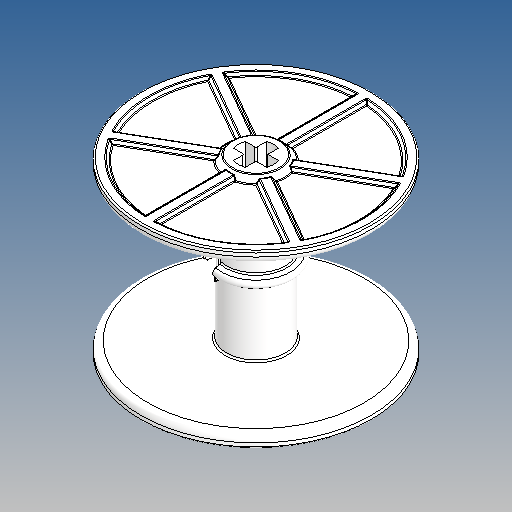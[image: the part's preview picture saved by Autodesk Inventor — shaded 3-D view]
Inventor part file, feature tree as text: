
AUTODESK INVENTOR PART (.ipt)
format: ipt  version: 2025 (Build 290162010, 162A)  size: 1,663,488 bytes
history: native  units: mm
features: fillet x5, sketch x4, extrude x3, pattern_circular x2, revolve x1, mirror x1
ambient origin geometry x8: Origin, YZ Plane, XZ Plane, XY Plane, X Axis, Y Axis, Z Axis, Center Point
bodies: Volumenkörper1 (feature_tree)
feature tree (16):
  revolve  "Umdrehung1"
  extrude  "Extrusion1"  Depth=8.0mm
  fillet  "Rundung1"  Radius=9.652752mm
  pattern_circular  "Runde Anordnung1"  [2 undecoded]
  fillet  "Rundung2"  Radius=0.75mm
  extrude  "Extrusion2"  Depth=10.0mm
  pattern_circular  "Runde Anordnung2"  [2 undecoded]
  fillet  "Rundung3"  Radius=1.2mm
  extrude  "Extrusion3"  TaperAngle=45.0deg  [1 undecoded]
  fillet  "Rundung4"  [1 undecoded]
  fillet  "Rundung5"  [1 undecoded]
  mirror  "Spiegeln1"
  sketch  "Skizze2"  dims[d0=12.0mm d1=8.0mm d2=9.652752mm]
  sketch  "Skizze3"  dims[d3=2.347248mm]
  sketch  "Skizze4"  dims[d4=31.4mm]
  sketch  "Skizze5"  dims[d5=11.65mm d6=0.4mm d7=0.75mm d8=10.0mm d9=0.296706mm d10=1.2mm d11=45.0deg d12=45.0deg d13=360.0deg d14=2.0mm d15=1.0mm d16=10.0mm d17=-7.853982mm d18=60.0mm d19=360.0deg d21=0.1mm d22=0.2mm d23=10.2mm d24=0.5mm d25=15.0deg d26=1.0mm d27=2.4mm d28=1.6mm d29=0.0mm d30=0.0mm d31=40.0mm d32=360.0deg d34=0.2mm d35=2.75mm d36=5.0mm d38=2.2mm d39=0.8mm d40=0.6mm d41=45.0deg d42=0.0mm d43=0.0mm d44=0.25mm d45=0.5mm d46=0.15mm]
note: 7 required parameter values undecoded (feature->parameter linkage not recoverable at this tier; creation-order binding heuristic only, values carry confidence <= 0.55)
